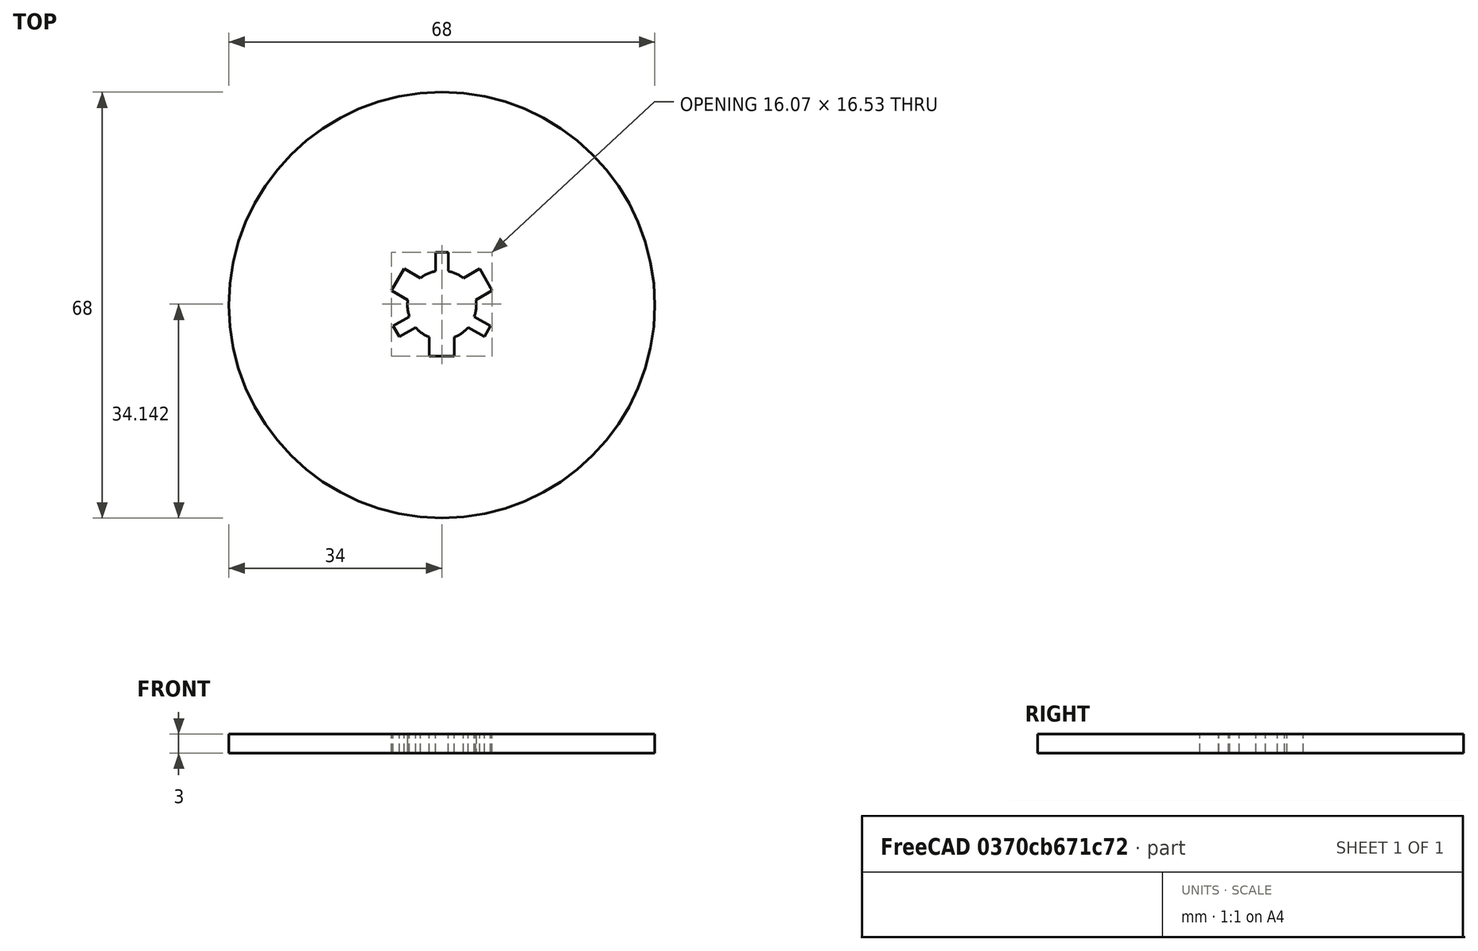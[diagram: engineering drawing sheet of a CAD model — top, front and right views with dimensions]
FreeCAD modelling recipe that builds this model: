
FCSTD DOCUMENT  (FreeCAD 0.21R30420 (Git))
Label: HeatpadHolder
License: All rights reserved
LicenseURL: http://en.wikipedia.org/wiki/All_rights_reserved
objects: Sketcher::SketchObject×1, PartDesign::Pad×1, PartDesign::Body×1
note: 4 computed .brp shape members not serialized (recipe doc carries the construction recipe); baked Part::Feature solids carry a one-line shape summary decoded from their .brp

FEATURE [Sketcher::SketchObject] Sketch
  FullyConstrained = true
  MapMode = 5
  Support = -> [XY_Plane]
  sketch-geometry (30):
    g0: Circle CenterX=0 CenterY=0 CenterZ=0 NormalX=0 NormalY=0 NormalZ=1 AngleXU=0 Radius=34
    g1: ArcOfCircle CenterX=0 CenterY=0 CenterZ=0 NormalX=0 NormalY=0 NormalZ=1 AngleXU=0 Radius=5.5 StartAngle=0.895767 EndAngle=1.38796
    g2: LineSegment StartX=-1 StartY=5.40833 StartZ=0 EndX=-1 EndY=8.40833 EndZ=0
    g3: LineSegment StartX=-1 StartY=8.40833 StartZ=0 EndX=1 EndY=8.40833 EndZ=0
    g4: LineSegment StartX=1 StartY=8.40833 StartZ=0 EndX=1 EndY=5.40833 EndZ=0
    g5: LineSegment StartX=5.18375 StartY=-1.83814 StartZ=0 EndX=7.78182 EndY=-3.33814 EndZ=0
    g6: LineSegment StartX=7.78182 StartY=-3.33814 StartZ=0 EndX=6.78182 EndY=-5.07019 EndZ=0
    g7: LineSegment StartX=6.78182 StartY=-5.07019 StartZ=0 EndX=4.18375 EndY=-3.57019 EndZ=0
    g8: LineSegment StartX=-4.18375 StartY=-3.57019 StartZ=0 EndX=-6.78182 EndY=-5.07019 EndZ=0
    g9: LineSegment StartX=-6.78182 StartY=-5.07019 StartZ=0 EndX=-7.78182 EndY=-3.33814 EndZ=0
    g10: LineSegment StartX=-7.78182 StartY=-3.33814 StartZ=0 EndX=-5.18375 EndY=-1.83814 EndZ=0
    g11: LineSegment StartX=3.43706 StartY=4.29379 StartZ=0 EndX=6.03514 EndY=5.79379 EndZ=0
    g12: LineSegment StartX=6.03514 StartY=5.79379 StartZ=0 EndX=8.03514 EndY=2.32969 EndZ=0
    g13: LineSegment StartX=8.03514 StartY=2.32969 StartZ=0 EndX=5.43706 EndY=0.829687 EndZ=0
    g14: LineSegment StartX=2 StartY=-5.12348 StartZ=0 EndX=2 EndY=-8.12348 EndZ=0
    g15: LineSegment StartX=2 StartY=-8.12348 StartZ=0 EndX=-2 EndY=-8.12348 EndZ=0
    g16: LineSegment StartX=-2 StartY=-8.12348 StartZ=0 EndX=-2 EndY=-5.12348 EndZ=0
    g17: LineSegment StartX=-5.43706 StartY=0.829687 StartZ=0 EndX=-8.03514 EndY=2.32969 EndZ=0
    g18: LineSegment StartX=-8.03514 StartY=2.32969 StartZ=0 EndX=-6.03514 EndY=5.79379 EndZ=0
    g19: LineSegment StartX=-6.03514 StartY=5.79379 StartZ=0 EndX=-3.43706 EndY=4.29379 EndZ=0
    g20: LineSegment StartX=-5.18375 StartY=-1.83814 StartZ=0 EndX=-4.18375 EndY=-3.57019 EndZ=0
    g21: LineSegment StartX=4.18375 StartY=-3.57019 StartZ=0 EndX=5.18375 EndY=-1.83814 EndZ=0
    g22: LineSegment StartX=-2 StartY=-5.12348 StartZ=0 EndX=2 EndY=-5.12348 EndZ=0
    g23: LineSegment StartX=-5.43706 StartY=0.829687 StartZ=0 EndX=-3.43706 EndY=4.29379 EndZ=0
    g24: LineSegment StartX=3.43706 StartY=4.29379 StartZ=0 EndX=5.43706 EndY=0.829687 EndZ=0
    g25: ArcOfCircle CenterX=0 CenterY=0 CenterZ=0 NormalX=0 NormalY=0 NormalZ=1 AngleXU=0 Radius=5.5 StartAngle=1.75363 EndAngle=2.24583
    g26: ArcOfCircle CenterX=0 CenterY=0 CenterZ=0 NormalX=0 NormalY=0 NormalZ=1 AngleXU=0 Radius=5.5 StartAngle=2.99016 EndAngle=3.48236
    g27: ArcOfCircle CenterX=0 CenterY=0 CenterZ=0 NormalX=0 NormalY=0 NormalZ=1 AngleXU=0 Radius=5.5 StartAngle=3.84803 EndAngle=4.34022
    g28: ArcOfCircle CenterX=0 CenterY=0 CenterZ=0 NormalX=0 NormalY=0 NormalZ=1 AngleXU=0 Radius=5.5 StartAngle=5.94242 EndAngle=6.43462
    g29: ArcOfCircle CenterX=0 CenterY=0 CenterZ=0 NormalX=0 NormalY=0 NormalZ=1 AngleXU=0 Radius=5.5 StartAngle=5.08456 EndAngle=5.57675
  constraints (91):
    c: Coincident(g0,g-1)
    c: Diameter(g0) = 68
    c: Coincident(g1,g0)
    c: Diameter(g1) = 11
    c: Vertical(g2)
    c: Coincident(g2,g3)
    c: Coincident(g3,g4)
    c: PointOnObject(g5,g1)
    c: Coincident(g5,g6)
    c: Coincident(g6,g7)
    c: PointOnObject(g7,g1)
    c: PointOnObject(g8,g1)
    c: Coincident(g8,g9)
    c: Coincident(g9,g10)
    c: PointOnObject(g10,g1)
    c: Coincident(g11,g12)
    c: Coincident(g12,g13)
    c: PointOnObject(g14,g1)
    c: Vertical(g14)
    c: Coincident(g14,g15)
    c: Horizontal(g15)
    c: Coincident(g15,g16)
    c: PointOnObject(g16,g1)
    c: PointOnObject(g17,g1)
    c: Coincident(g17,g18)
    c: Coincident(g18,g19)
    c: PointOnObject(g19,g1)
    c: Vertical(g4)
    c: Symmetric(g3,g2,g-2)
    c: Distance(g3,g2) = 2
    c: DistanceY(g4,g4) = 3
    c: Angle(g10) = 0.523599
    c: Parallel(g10,g8)
    c: Perpendicular(g8,g9)
    c: Coincident(g20,g10)
    c: Perpendicular(g10,g20)
    c: Coincident(g20,g8)
    c: Distance(g9,g8) = 2
    c: Distance(g10) = 3
    c: Angle(g5) = -0.523599
    c: Perpendicular(g5,g6)
    c: Coincident(g21,g7)
    c: Coincident(g21,g5)
    c: Perpendicular(g7,g21)
    c: Distance(g6) = 2
    c: Parallel(g5,g7)
    c: Distance(g7) = 3
    c: Distance(g15) = 4
    c: Parallel(g16,g14)
    c: Distance(g16) = 3
    c: Coincident(g22,g16)
    c: Coincident(g22,g14)
    c: Parallel(g22,g15)
    c: Angle(g17) = 2.61799
    c: Parallel(g17,g19)
    c: Coincident(g23,g17)
    c: Coincident(g23,g19)
    c: Parallel(g23,g18)
    c: Distance(g18) = 4
    c: Distance(g17) = 3
    c: Perpendicular(g19,g18)
    c: Perpendicular(g12,g11)
    c: Distance(g12) = 4
    c: Distance(g11) = 3
    c: Coincident(g24,g11)
    c: Coincident(g24,g13)
    c: Parallel(g24,g12)
    c: Parallel(g13,g11)
    c: Angle(g11) = 0.523599
    c: Coincident(g28,g13)
    c: Coincident(g1,g11)
    c: Equal(g1,g25)
    c: Coincident(g1,g4)
    c: Coincident(g25,g2)
    c: Coincident(g1,g25)
    c: Equal(g25,g26)
    c: PointOnObject(g25,g19)
    c: PointOnObject(g26,g17)
    c: Coincident(g25,g26)
    c: Equal(g26,g27)
    c: PointOnObject(g26,g20)
    c: PointOnObject(g27,g8)
    c: Coincident(g26,g27)
    c: Equal(g27,g28)
    c: PointOnObject(g29,g7)
    c: PointOnObject(g28,g21)
    c: Coincident(g27,g28)
    c: Equal(g27,g29)
    c: PointOnObject(g27,g16)
    c: PointOnObject(g29,g14)
    c: Coincident(g27,g29)
FEATURE [PartDesign::Pad] Pad
  Direction = (0,0,1)
  Length = 3
  Length2 = 10
  Profile = -> Sketch
  ReferenceAxis = -> Sketch [N_Axis]
  Type = 0
FEATURE [PartDesign::Body] Body
  Group = -> [Sketch,Pad]
  Origin = -> Origin
  Tip = -> Pad
